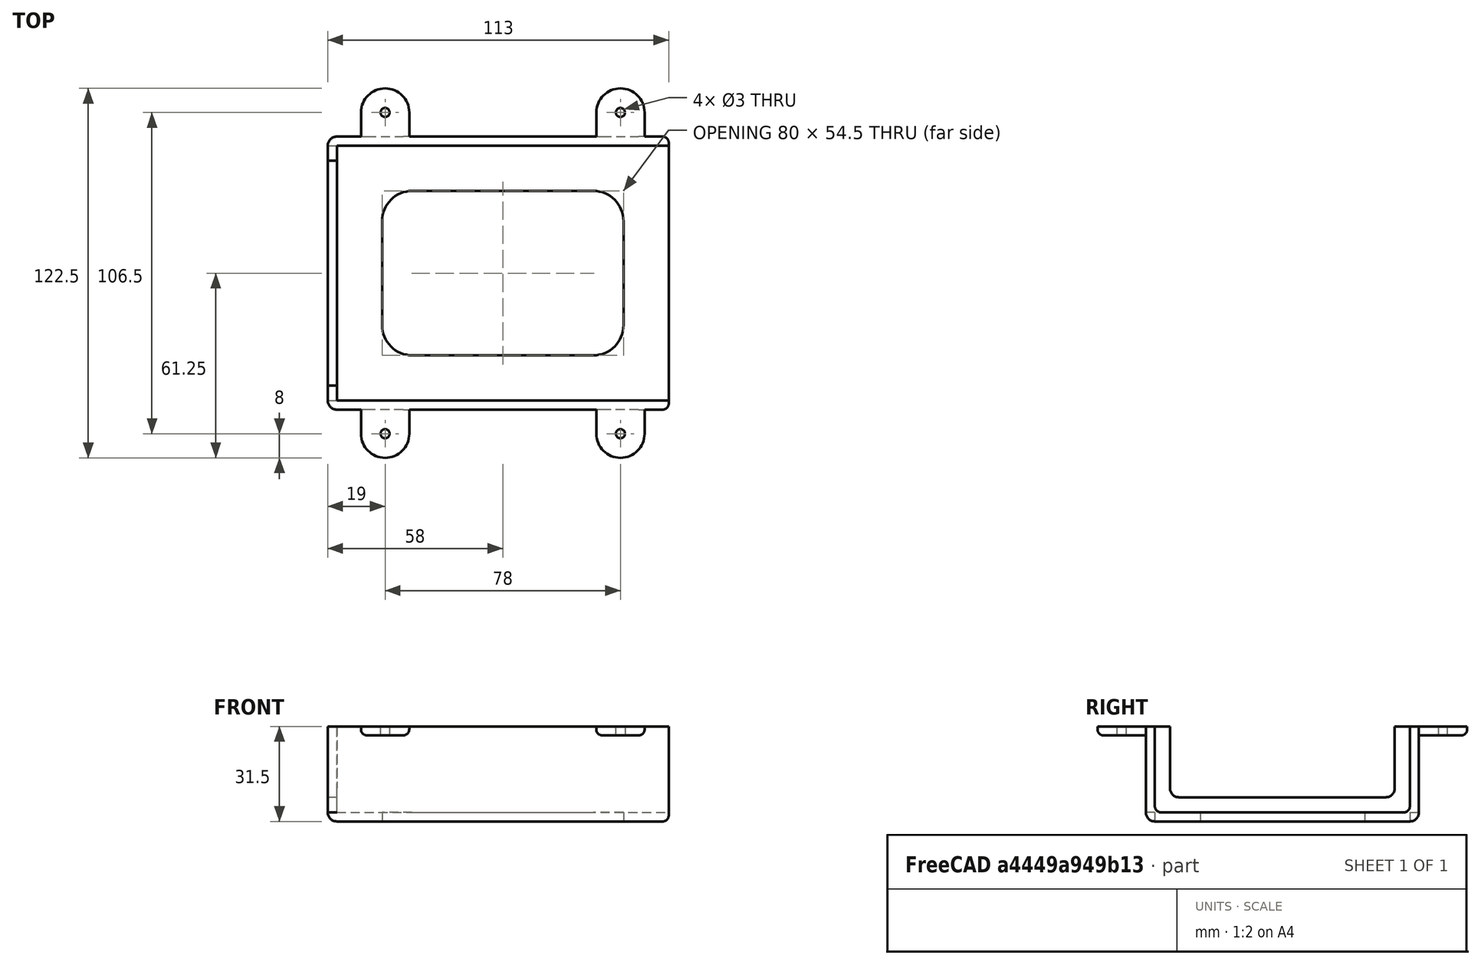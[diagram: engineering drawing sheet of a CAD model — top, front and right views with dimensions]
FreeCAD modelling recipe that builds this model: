
FCSTD DOCUMENT  (FreeCAD 0.21R33668 +7 (Git))
Label: UnderTableBracket
License: All rights reserved
LicenseURL: http://en.wikipedia.org/wiki/All_rights_reserved
objects: Sketcher::SketchObject×3, PartDesign::Fillet×3, PartDesign::Pocket×2, Spreadsheet::Sheet×1, PartDesign::AdditiveBox×1, PartDesign::Thickness×1, PartDesign::Pad×1, PartDesign::LinearPattern×1, PartDesign::Plane×1, PartDesign::Mirrored×1, PartDesign::MultiTransform×1, PartDesign::Body×1, App::Part×1, Mesh::Feature×1
note: 24 computed .brp shape members not serialized (recipe doc carries the construction recipe); baked Part::Feature solids carry a one-line shape summary decoded from their .brp

FEATURE [Spreadsheet::Sheet] Spreadsheet
  cells = A1='Width; B1(Width)=84.5; A2='Height; B2(Height)=28.5; A3='Depth; B3(Depth)=110; A4='Screw Diameter; B4(ScrewDiameter)=3
FEATURE [PartDesign::AdditiveBox] Box
  AttacherType = Attacher::AttachEngine3D
  Height = 28.5
  Length = 110
  Width = 84.5
  expr: Height = Spreadsheet.Height
  expr: Length = Spreadsheet.Depth
  expr: Width = Spreadsheet.Width
FEATURE [PartDesign::Thickness] Thickness
  Base = -> Box [Face6,Face2]
  BaseFeature = -> Box
  Intersection = false
  Join = 0
  Mode = 0
  SupportTransform = false
  Value = 3
FEATURE [Sketcher::SketchObject] Sketch
  ExternalGeometry = -> [Thickness]
  FullyConstrained = false
  MapMode = 5
  Placement = pos=(0,0,0) rot=(0.57735,0.57735,0.57735;2.0944rad)
  Support = -> [Thickness]
  sketch-geometry (8):
    g0: LineSegment StartX=79.5 StartY=28.5 StartZ=0 EndX=79.5 EndY=8 EndZ=0
    g1: ArcOfCircle CenterX=76.5 CenterY=8 CenterZ=0 NormalX=0 NormalY=0 NormalZ=1 AngleXU=0 Radius=3 StartAngle=4.71239 EndAngle=6.28319
    g2: LineSegment StartX=76.5 StartY=5 StartZ=0 EndX=8 EndY=5 EndZ=0
    g3: ArcOfCircle CenterX=8 CenterY=8 CenterZ=0 NormalX=0 NormalY=0 NormalZ=1 AngleXU=0 Radius=3 StartAngle=3.14159 EndAngle=4.71239
    g4: LineSegment StartX=5 StartY=8 StartZ=0 EndX=5 EndY=28.5 EndZ=0
    g5: GeomPoint X=5 Y=35.516 Z=0
    g6: GeomPoint X=79.5 Y=5 Z=0
    g7: LineSegment StartX=5 StartY=28.5 StartZ=0 EndX=79.5 EndY=28.5 EndZ=0
  constraints (19):
    c: Tangent(g0,g1) = 1.5708
    c: Tangent(g1,g2) = 1.5708
    c: Tangent(g2,g3) = 1.5708
    c: Tangent(g3,g4) = 1.5708
    c: Horizontal(g2)
    c: Vertical(g0)
    c: Vertical(g4)
    c: Equal(g1,g3)
    c: PointOnObject(g5,g4)
    c: PointOnObject(g6,g0)
    c: PointOnObject(g6,g2)
    c: PointOnObject(g4,g-3)
    c: PointOnObject(g0,g-3)
    c: Radius(g3) = 3
    c: DistanceX(g-3,g4) = 5
    c: DistanceX(g0,g-3) = 5
    c: DistanceY(g-1,g2) = 5
    c: Coincident(g7,g4)
    c: Coincident(g7,g0)
FEATURE [PartDesign::Pocket] Pocket
  BaseFeature = -> Thickness
  Direction = (-1,0,0)
  Length = 5
  Length2 = 5
  Profile = -> Sketch
  ReferenceAxis = -> Sketch [N_Axis]
  Type = 1
FEATURE [Sketcher::SketchObject] Sketch001
  ExternalGeometry = -> [Pocket]
  FullyConstrained = true
  MapMode = 5
  Support = -> [Pocket]
  sketch-geometry (10):
    g0: ArcOfCircle CenterX=25 CenterY=59.5 CenterZ=0 NormalX=0 NormalY=0 NormalZ=1 AngleXU=0 Radius=10 StartAngle=1.5708 EndAngle=3.14159
    g1: LineSegment StartX=25 StartY=69.5 StartZ=0 EndX=85 EndY=69.5 EndZ=0
    g2: ArcOfCircle CenterX=85 CenterY=59.5 CenterZ=0 NormalX=0 NormalY=0 NormalZ=1 AngleXU=0 Radius=10 StartAngle=0 EndAngle=1.5708
    g3: LineSegment StartX=95 StartY=59.5 StartZ=0 EndX=95 EndY=25 EndZ=0
    g4: ArcOfCircle CenterX=85 CenterY=25 CenterZ=0 NormalX=0 NormalY=0 NormalZ=1 AngleXU=0 Radius=10 StartAngle=4.71239 EndAngle=6.28319
    g5: LineSegment StartX=85 StartY=15 StartZ=0 EndX=25 EndY=15 EndZ=0
    g6: ArcOfCircle CenterX=25 CenterY=25 CenterZ=0 NormalX=0 NormalY=0 NormalZ=1 AngleXU=0 Radius=10 StartAngle=3.14159 EndAngle=4.71239
    g7: LineSegment StartX=15 StartY=25 StartZ=0 EndX=15 EndY=59.5 EndZ=0
    g8: GeomPoint X=15 Y=69.5 Z=0
    g9: GeomPoint X=95 Y=15 Z=0
  constraints (24):
    c: Tangent(g0,g1) = 1.5708
    c: Tangent(g1,g2) = 1.5708
    c: Tangent(g2,g3) = 1.5708
    c: Tangent(g3,g4) = 1.5708
    c: Tangent(g4,g5) = 1.5708
    c: Tangent(g5,g6) = 1.5708
    c: Tangent(g6,g7) = 1.5708
    c: Tangent(g7,g0) = 1.5708
    c: Horizontal(g1)
    c: Horizontal(g5)
    c: Vertical(g3)
    c: Vertical(g7)
    c: Equal(g0,g2)
    c: Equal(g2,g4)
    c: Equal(g4,g6)
    c: PointOnObject(g8,g1)
    c: PointOnObject(g8,g7)
    c: PointOnObject(g9,g3)
    c: PointOnObject(g9,g5)
    c: Radius(g2) = 10
    c: DistanceY(g1,g-4) = 15
    c: DistanceY(g-4,g4) = 15
    c: DistanceX(g3,g-4) = 15
    c: DistanceX(g-3,g0) = 15
FEATURE [PartDesign::Pocket] Pocket001
  BaseFeature = -> Pocket
  Direction = (0,0,-1)
  Length = 5
  Length2 = 5
  Profile = -> Sketch001
  ReferenceAxis = -> Sketch001 [N_Axis]
  Type = 1
FEATURE [PartDesign::Fillet] Fillet
  Base = -> Pocket001 [Edge32,Edge34]
  BaseFeature = -> Pocket001
  Radius = 2
  SupportTransform = false
  UseAllEdges = false
FEATURE [Sketcher::SketchObject] Sketch002
  ExternalGeometry = -> [Box]
  FullyConstrained = true
  MapMode = 5
  Placement = pos=(0,0,28.5) rot=(0,0,1;0rad)
  Support = -> [Box]
  expr: Constraints[10] = Spreadsheet.ScrewDiameter
  sketch-geometry (5):
    g0: ArcOfCircle CenterX=16 CenterY=95.5 CenterZ=0 NormalX=0 NormalY=0 NormalZ=1 AngleXU=0 Radius=8 StartAngle=0 EndAngle=3.14159
    g1: LineSegment StartX=8 StartY=95.5 StartZ=0 EndX=8 EndY=84.5 EndZ=0
    g2: LineSegment StartX=24 StartY=84.5 StartZ=0 EndX=24 EndY=95.5 EndZ=0
    g3: Circle CenterX=16 CenterY=95.5 CenterZ=0 NormalX=0 NormalY=0 NormalZ=1 AngleXU=0 Radius=1.5
    g4: LineSegment StartX=8 StartY=84.5 StartZ=0 EndX=24 EndY=84.5 EndZ=0
  constraints (13):
    c: Tangent(g0,g1) = -1.5708
    c: Tangent(g2,g0) = -1.5708
    c: Vertical(g1)
    c: PointOnObject(g1,g-3)
    c: PointOnObject(g2,g-3)
    c: Radius(g0) = 8
    c: Vertical(g2)
    c: DistanceY(g2,g2) = 11
    c: DistanceX(g-3,g1) = 8
    c: Coincident(g3,g0)
    c: Diameter(g3) = 3
    c: Coincident(g4,g1)
    c: Coincident(g4,g2)
FEATURE [PartDesign::Pad] Pad
  BaseFeature = -> Fillet
  Direction = (0,0,1)
  Length = 3
  Length2 = 10
  Profile = -> Sketch002
  ReferenceAxis = -> Sketch002 [N_Axis]
  Reversed = true
  Type = 0
FEATURE [PartDesign::LinearPattern] LinearPattern
  Direction = -> Sketch002 [H_Axis]
  Length = 78
  Occurrences = 2
  expr: Length = Spreadsheet.Depth - 32
FEATURE [PartDesign::Plane] DatumPlane
  AttachmentOffset = pos=(0,0,0) rot=(0.57735,0.57735,0.57735;2.0944rad)
  Length = 151.997
  MapMode = 45
  Placement = pos=(55,42.25,14.25) rot=(0,0.707107,0.707107;3.14159rad)
  ResizeMode = 0
  Support = -> [Box]
  Width = 70.4971
FEATURE [PartDesign::Mirrored] Mirrored
  MirrorPlane = -> DatumPlane
FEATURE [PartDesign::MultiTransform] MultiTransform
  BaseFeature = -> Pad
  Originals = -> [Pad]
  Transformations = -> [LinearPattern,Mirrored]
FEATURE [PartDesign::Fillet] Fillet001
  Base = -> MultiTransform [Edge168,Edge169,Edge167,Edge161,Edge162,Edge160,Edge137,Edge139,Edge138,Edge145,Edge147,Edge146]
  BaseFeature = -> MultiTransform
  Radius = 2
  SupportTransform = false
  UseAllEdges = false
FEATURE [PartDesign::Fillet] Fillet002
  Base = -> Fillet001 [Edge37,Edge36,Edge34,Edge32,Edge5]
  BaseFeature = -> Fillet001
  Radius = 2
  SupportTransform = false
  UseAllEdges = false
FEATURE [PartDesign::Body] Body
  Group = -> [Box,Thickness,Sketch,Pocket,Sketch001,Pocket001,Fillet,Sketch002,Pad,MultiTransform,LinearPattern,DatumPlane,Mirrored,Fillet001,Fillet002]
  Origin = -> Origin001
  Tip = -> Fillet002
FEATURE [App::Part] Part  label="Bracket"
  Group = -> [Body]
  Origin = -> Origin
FEATURE [Mesh::Feature] Mesh  label="Fillet002 (Meshed)"
